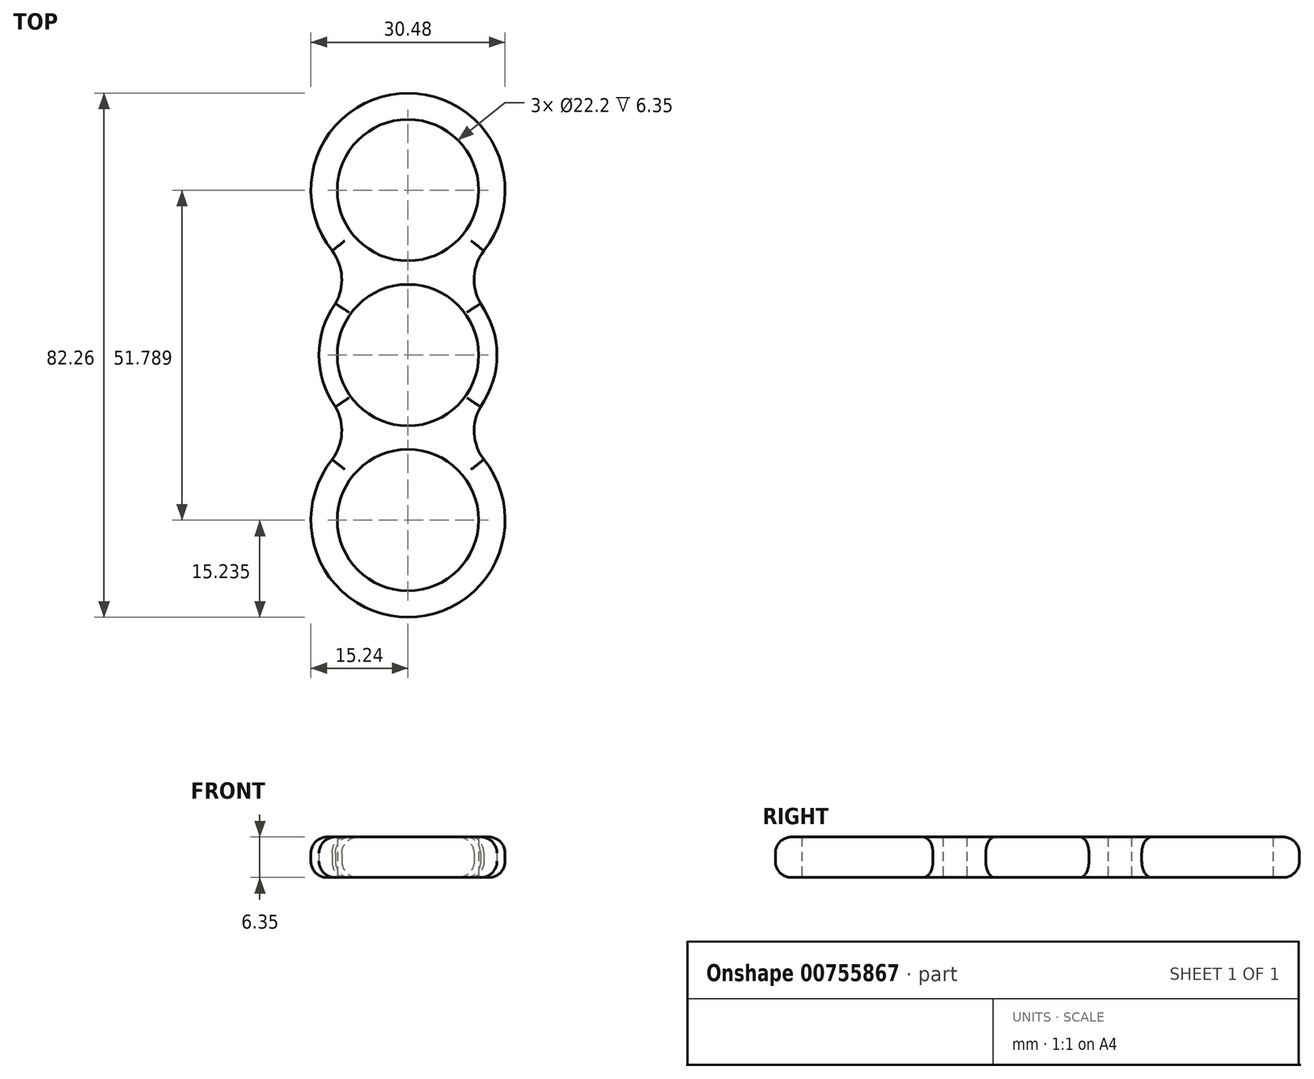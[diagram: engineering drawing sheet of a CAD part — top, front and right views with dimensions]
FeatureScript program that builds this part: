
annotation { "Feature Type Name" : "Feature", "Feature Type Description" : "" }
export const myFeature = defineFeature(function(context is Context, id is Id, definition is map)
    precondition{}
    {
        {
            var Q0;
            Q0=qCreatedBy(makeId("Top.planeOp"),FACE);
            var sketch = newSketch(context, id + "F0", { "sketchPlane" : qUnion([Q0])});
            skArc(sketch, "E0", {"start": v(-11.39, 8.09) * mm, "mid": v(-13.97, 0) * mm, "end": v(-11.39, -8.09) * mm});
            skCircle(sketch, "E1", {"center": v(0, 25.9) * mm, "radius": 11.1 * mm});
            skArc(sketch, "E2", {"start": v(11.9, 16.39) * mm, "mid": v(0, 41.13) * mm, "end": v(-11.9, 16.39) * mm});
            skCircle(sketch, "E3.1.0", {"center": v(0, -25.9) * mm, "radius": 11.1 * mm});
            skArc(sketch, "E3.1.1", {"start": v(-11.9, -16.39) * mm, "mid": v(0, -41.13) * mm, "end": v(11.9, -16.39) * mm});
            skArc(sketch, "E4.trimOffspring", {"start": v(11.39, -8.09) * mm, "mid": v(13.97, 0) * mm, "end": v(11.39, 8.09) * mm});
            skPoint(sketch, "E5.orphan", {"position": v(6.75, 12.23) * mm});
            skArc(sketch, "E6.1.0", {"start": v(11.39, -8.09) * mm, "mid": v(10.4, -12.32) * mm, "end": v(11.9, -16.39) * mm});
            skPoint(sketch, "E7.orphan", {"position": v(-6.75, 12.23) * mm});
            skPoint(sketch, "E8.orphan", {"position": v(-6.75, -12.23) * mm});
            skPoint(sketch, "E9.orphan", {"position": v(6.75, -12.23) * mm});
            skCircle(sketch, "E10", {"center": v(0, 0) * mm, "radius": 11.1 * mm});
            skArc(sketch, "E11", {"start": v(-11.9, -16.39) * mm, "mid": v(-10.4, -12.32) * mm, "end": v(-11.39, -8.09) * mm});
            skArc(sketch, "E12.1.0", {"start": v(-11.39, 8.09) * mm, "mid": v(-10.4, 12.32) * mm, "end": v(-11.9, 16.39) * mm});
            skArc(sketch, "E12.1.1", {"start": v(11.9, 16.39) * mm, "mid": v(10.4, 12.32) * mm, "end": v(11.39, 8.09) * mm});
            skSolve(sketch);
        }
        {
            var Q0;
            Q0=qSketchRegion(id+"F0",true);
            extrude(context, id + "F1", {"entities" : qUnion([Q0]), "depth" : 6.35 * mm, "offsetDistance" : 25.4 * mm});
        }
        {
            var Q0;
            Q0=makeQuery(id+"F1.opExtrude","CAP_EDGE",EDGE,{"disambiguationData":[OSD([sQuery(id+"F0.wireOp",EDGE,"trfGYVC9-aXAH-ZeNA-1ujl-99YJ1Eel9iI7")])],"isStart":false});
            var Q1;
            Q1=makeQuery(id+"F1.opExtrude","CAP_EDGE",EDGE,{"disambiguationData":[OSD([sQuery(id+"F0.wireOp",EDGE,"E2")])],"isStart":false});
            var Q2;
            Q2=makeQuery(id+"F1.opExtrude","CAP_EDGE",EDGE,{"disambiguationData":[OSD([sQuery(id+"F0.wireOp",EDGE,"s0x0RKGQ-nikB-3b35-0FTQ-KnRF4wtLLO6Y")])],"isStart":false});
            var Q3;
            Q3=makeQuery(id+"F1.opExtrude","CAP_EDGE",EDGE,{"disambiguationData":[OSD([sQuery(id+"F0.wireOp",EDGE,"E4.trimOffspring")])],"isStart":false});
            var Q4;
            Q4=makeQuery(id+"F1.opExtrude","CAP_EDGE",EDGE,{"disambiguationData":[OSD([sQuery(id+"F0.wireOp",EDGE,"E0")])],"isStart":false});
            var Q5;
            Q5=makeQuery(id+"F1.opExtrude","CAP_EDGE",EDGE,{"disambiguationData":[OSD([sQuery(id+"F0.wireOp",EDGE,"2800c864-b789-4809-b79f-413da69f2f8b.1.0")])],"isStart":false});
            var Q6;
            Q6=makeQuery(id+"F1.opExtrude","CAP_EDGE",EDGE,{"disambiguationData":[OSD([sQuery(id+"F0.wireOp",EDGE,"E3.1.1")])],"isStart":false});
            var Q7;
            Q7=makeQuery(id+"F1.opExtrude","CAP_EDGE",EDGE,{"disambiguationData":[OSD([sQuery(id+"F0.wireOp",EDGE,"E6.1.0")])],"isStart":false});
            var Q8;
            Q8=makeQuery(id+"F1.opExtrude","CAP_EDGE",EDGE,{"disambiguationData":[OSD([sQuery(id+"F0.wireOp",EDGE,"E3.1.1")])],"isStart":true});
            var Q9;
            Q9=makeQuery(id+"F1.opExtrude","CAP_EDGE",EDGE,{"disambiguationData":[OSD([sQuery(id+"F0.wireOp",EDGE,"E6.1.0")])],"isStart":true});
            var Q10;
            Q10=makeQuery(id+"F1.opExtrude","CAP_EDGE",EDGE,{"disambiguationData":[OSD([sQuery(id+"F0.wireOp",EDGE,"2800c864-b789-4809-b79f-413da69f2f8b.1.0")])],"isStart":true});
            var Q11;
            Q11=makeQuery(id+"F1.opExtrude","CAP_EDGE",EDGE,{"disambiguationData":[OSD([sQuery(id+"F0.wireOp",EDGE,"E0")])],"isStart":true});
            var Q12;
            Q12=makeQuery(id+"F1.opExtrude","CAP_EDGE",EDGE,{"disambiguationData":[OSD([sQuery(id+"F0.wireOp",EDGE,"E4.trimOffspring")])],"isStart":true});
            var Q13;
            Q13=makeQuery(id+"F1.opExtrude","CAP_EDGE",EDGE,{"disambiguationData":[OSD([sQuery(id+"F0.wireOp",EDGE,"s0x0RKGQ-nikB-3b35-0FTQ-KnRF4wtLLO6Y")])],"isStart":true});
            var Q14;
            Q14=makeQuery(id+"F1.opExtrude","CAP_EDGE",EDGE,{"disambiguationData":[OSD([sQuery(id+"F0.wireOp",EDGE,"trfGYVC9-aXAH-ZeNA-1ujl-99YJ1Eel9iI7")])],"isStart":true});
            var Q15;
            Q15=makeQuery(id+"F1.opExtrude","CAP_EDGE",EDGE,{"disambiguationData":[OSD([sQuery(id+"F0.wireOp",EDGE,"E2")])],"isStart":true});
            fillet(context, id + "F2", {"entities" : qUnion([Q0, Q1, Q2, Q3, Q4, Q5, Q6, Q7, Q8, Q9, Q10, Q11, Q12, Q13, Q14, Q15]), "radius" : 2.54 * mm, "tangentPropagation" : true, "allowEdgeOverflow" : false});
        }
        {
            var Q0;
            Q0=qSketchRegion(id+"F0",true);
            extrude(context, id + "F3", {"entities" : qUnion([Q0]), "operationType" : NewBodyOperationType.ADD, "depth" : 6.35 * mm, "offsetDistance" : 25.4 * mm});
        }
        {
            var Q0;
            Q0=makeQuery(id+"F3.opExtrude","CAP_EDGE",EDGE,{"disambiguationData":[OSD([sQuery(id+"F0.wireOp",EDGE,"E2")])],"isStart":false});
            var Q1;
            Q1=makeQuery(id+"F3.opExtrude","CAP_EDGE",EDGE,{"disambiguationData":[OSD([sQuery(id+"F0.wireOp",EDGE,"E12.1.0")])],"isStart":false});
            var Q2;
            Q2=makeQuery(id+"F3.opExtrude","CAP_EDGE",EDGE,{"disambiguationData":[OSD([sQuery(id+"F0.wireOp",EDGE,"E0")])],"isStart":false});
            var Q3;
            Q3=makeQuery(id+"F3.opExtrude","CAP_EDGE",EDGE,{"disambiguationData":[OSD([sQuery(id+"F0.wireOp",EDGE,"E3.1.1")])],"isStart":false});
            var Q4;
            Q4=makeQuery(id+"F3.opExtrude","CAP_EDGE",EDGE,{"disambiguationData":[OSD([sQuery(id+"F0.wireOp",EDGE,"E11")])],"isStart":false});
            var Q5;
            Q5=makeQuery(id+"F3.opExtrude","CAP_EDGE",EDGE,{"disambiguationData":[OSD([sQuery(id+"F0.wireOp",EDGE,"E6.1.0")])],"isStart":false});
            var Q6;
            Q6=makeQuery(id+"F3.opExtrude","CAP_EDGE",EDGE,{"disambiguationData":[OSD([sQuery(id+"F0.wireOp",EDGE,"E4.trimOffspring")])],"isStart":false});
            var Q7;
            Q7=makeQuery(id+"F3.opExtrude","CAP_EDGE",EDGE,{"disambiguationData":[OSD([sQuery(id+"F0.wireOp",EDGE,"E12.1.1")])],"isStart":false});
            fillet(context, id + "F4", {"entities" : qUnion([Q0, Q1, Q2, Q3, Q4, Q5, Q6, Q7]), "radius" : 2.54 * mm, "tangentPropagation" : true, "allowEdgeOverflow" : false});
        }
        {
            var Q0;
            Q0=makeQuery(id+"F3.opExtrude","CAP_EDGE",EDGE,{"disambiguationData":[OSD([sQuery(id+"F0.wireOp",EDGE,"E3.1.1")])],"isStart":true});
            var Q1;
            Q1=makeQuery(id+"F3.opExtrude","CAP_EDGE",EDGE,{"disambiguationData":[OSD([sQuery(id+"F0.wireOp",EDGE,"E2")])],"isStart":true});
            var Q2;
            Q2=makeQuery(id+"F3.opExtrude","CAP_EDGE",EDGE,{"disambiguationData":[OSD([sQuery(id+"F0.wireOp",EDGE,"E0")])],"isStart":true});
            var Q3;
            Q3=makeQuery(id+"F3.opExtrude","CAP_EDGE",EDGE,{"disambiguationData":[OSD([sQuery(id+"F0.wireOp",EDGE,"E4.trimOffspring")])],"isStart":true});
            var Q4;
            Q4=makeQuery(id+"F3.opExtrude","CAP_EDGE",EDGE,{"disambiguationData":[OSD([sQuery(id+"F0.wireOp",EDGE,"E12.1.1")])],"isStart":true});
            var Q5;
            Q5=makeQuery(id+"F3.opExtrude","CAP_EDGE",EDGE,{"disambiguationData":[OSD([sQuery(id+"F0.wireOp",EDGE,"E12.1.0")])],"isStart":true});
            var Q6;
            Q6=makeQuery(id+"F3.opExtrude","CAP_EDGE",EDGE,{"disambiguationData":[OSD([sQuery(id+"F0.wireOp",EDGE,"E11")])],"isStart":true});
            var Q7;
            Q7=makeQuery(id+"F3.opExtrude","CAP_EDGE",EDGE,{"disambiguationData":[OSD([sQuery(id+"F0.wireOp",EDGE,"E6.1.0")])],"isStart":true});
            fillet(context, id + "F5", {"entities" : qUnion([Q0, Q1, Q2, Q3, Q4, Q5, Q6, Q7]), "radius" : 2.54 * mm, "tangentPropagation" : true, "allowEdgeOverflow" : false});
        }
    });
